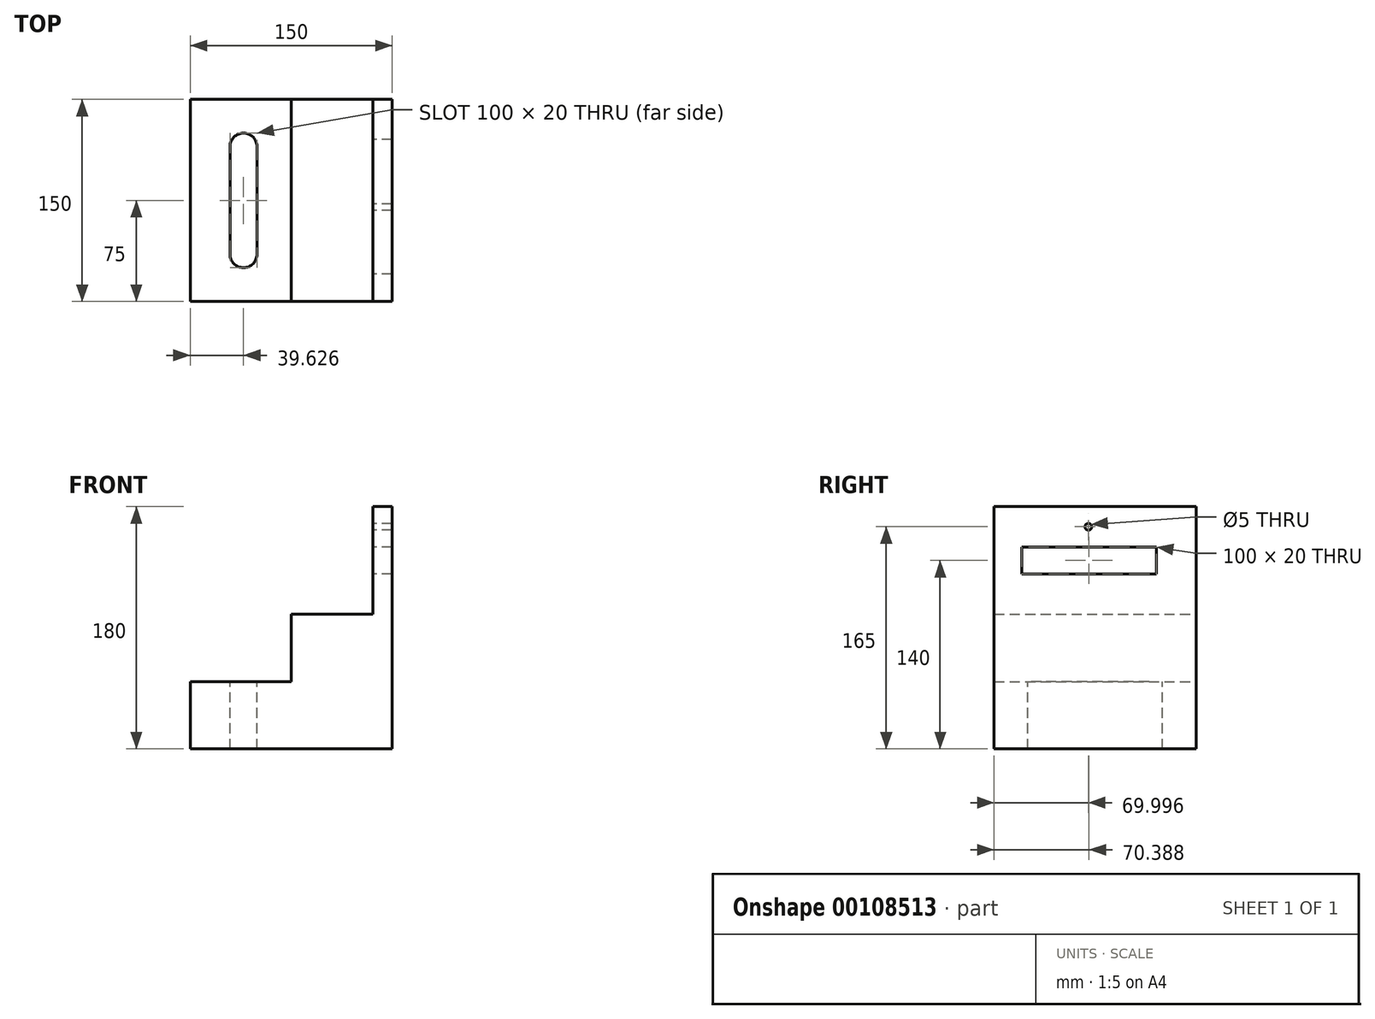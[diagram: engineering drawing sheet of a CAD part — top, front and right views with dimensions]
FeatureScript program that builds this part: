
annotation { "Feature Type Name" : "Feature", "Feature Type Description" : "" }
export const myFeature = defineFeature(function(context is Context, id is Id, definition is map)
    precondition{}
    {
        {
            var Q0;
            Q0=qCreatedBy(makeId("Front.planeOp"),FACE);
            var sketch = newSketch(context, id + "F0", { "sketchPlane" : qUnion([Q0])});
            skLineSegment(sketch, "E0.bottom", {"start": v(75, -90) * mm, "end": v(-75, -90) * mm});
            skLineSegment(sketch, "E0.top", {"start": v(75, 90) * mm, "end": v(60.69, 90) * mm});
            skLineSegment(sketch, "E0.left", {"start": v(75, -90) * mm, "end": v(75, 90) * mm});
            skLineSegment(sketch, "E0.right", {"start": v(-75, -90) * mm, "end": v(-75, -40) * mm});
            skPoint(sketch, "E0.middle", {"position": v(0, 0) * mm});
            skLineSegment(sketch, "E1", {"start": v(60.69, 90) * mm, "end": v(60.69, 10) * mm});
            skLineSegment(sketch, "E2", {"start": v(60.69, 10) * mm, "end": v(0, 10) * mm});
            skLineSegment(sketch, "E3", {"start": v(0, 10) * mm, "end": v(0, -40) * mm});
            skLineSegment(sketch, "E4", {"start": v(0, -40) * mm, "end": v(-75, -40) * mm});
            skPoint(sketch, "E5.orphan", {"position": v(-75, 90) * mm});
            skSolve(sketch);
        }
        {
            var Q0;
            Q0 = qSketchRegion(id + "F0", true);
            extrude(context, id + "F1", {"entities" : qUnion([Q0]), "depth" : 150 * mm});
        }
        {
            var Q0;
            Q0=makeQuery(id+"F1.opExtrude","SWEPT_FACE",FACE,{"disambiguationData":[OSD([sQuery(id+"F0.wireOp",EDGE,"E4")])]});
            var sketch = newSketch(context, id + "F2", { "sketchPlane" : qUnion([Q0])});
            skLineSegment(sketch, "E6.left", {"start": v(-25.37, -35) * mm, "end": v(-25.37, -115) * mm});
            skLineSegment(sketch, "E6.right", {"start": v(-45.37, -35) * mm, "end": v(-45.37, -115) * mm});
            skCircle(sketch, "E7", {"center": v(-35.37, -115) * mm, "radius": 10 * mm});
            skCircle(sketch, "E8", {"center": v(-35.37, -35) * mm, "radius": 10 * mm});
            skPoint(sketch, "E9", {"position": v(-45.37, -75) * mm});
            skPoint(sketch, "E10", {"position": v(-75, -75) * mm});
            skSolve(sketch);
        }
        {
            var Q0;
            Q0 = qSketchRegion(id + "F2", true);
            extrude(context, id + "F3", {"entities" : qUnion([Q0]), "operationType" : NewBodyOperationType.REMOVE, "endBound" : BoundingType.THROUGH_ALL, "oppositeDirection" : true, "depth" : 25 * mm});
        }
        {
            var Q0;
            Q0=makeQuery(id+"F1.opExtrude","SWEPT_FACE",FACE,{"disambiguationData":[OSD([sQuery(id+"F0.wireOp",EDGE,"E1")])]});
            var sketch = newSketch(context, id + "F4", { "sketchPlane" : qUnion([Q0])});
            skLineSegment(sketch, "E11.bottom", {"start": v(129.61, 60) * mm, "end": v(29.61, 60) * mm});
            skLineSegment(sketch, "E11.top", {"start": v(129.61, 40) * mm, "end": v(29.61, 40) * mm});
            skLineSegment(sketch, "E11.left", {"start": v(129.61, 60) * mm, "end": v(129.61, 40) * mm});
            skLineSegment(sketch, "E11.right", {"start": v(29.61, 60) * mm, "end": v(29.61, 40) * mm});
            skCircle(sketch, "E12", {"center": v(80, 75) * mm, "radius": 2.5 * mm});
            skSolve(sketch);
        }
        {
            var Q0;
            Q0=makeQuery(id+"F4.imprint","IMPRINT",FACE,{"disambiguationData":[TD([[makeQuery(id+"F4.imprint","IMPRINT",EDGE,{"derivedFrom":sQuery(id+"F4.wireOp",EDGE,"E11.bottom")}),1.0]])]});
            var Q1;
            Q1=makeQuery(id+"F4.imprint","IMPRINT",FACE,{"disambiguationData":[TD([[makeQuery(id+"F4.imprint","IMPRINT",EDGE,{"derivedFrom":sQuery(id+"F4.wireOp",EDGE,"E12")}),1.0]])]});
            extrude(context, id + "F5", {"entities" : qUnion([Q0, Q1]), "operationType" : NewBodyOperationType.REMOVE, "endBound" : BoundingType.THROUGH_ALL, "oppositeDirection" : true, "depth" : 25 * mm});
        }
    });
